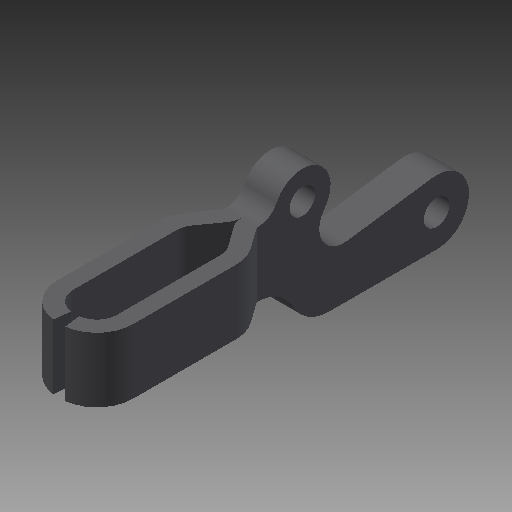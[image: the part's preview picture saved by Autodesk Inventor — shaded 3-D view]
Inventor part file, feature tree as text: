
AUTODESK INVENTOR PART (.ipt)
format: ipt  version: 2018 (Build 220112000, 112)  size: 174,592 bytes
history: native  units: mm
features: other x35, sketch x4, extrude x2, revolve x2
ambient origin geometry x8: Origin, YZ Plane, XZ Plane, XY Plane, X Axis, Y Axis, Z Axis, Center Point
bodies: Solid1 (feature_tree)
feature tree (43):
  extrude  "Extrusion1"  Depth=40.0mm TaperAngle=0.0deg
  extrude  "Extrusion2"  TaperAngle=360.0deg  [1 undecoded]
  revolve  "Revolution1"  [1 undecoded]
  revolve  "Revolution2"  [1 undecoded]
  other  "P1_XY"
  other  "P1_YZ"
  other  "P1_ZX"
  other  "P1_X"
  other  "P1_Y"
  other  "P1_Z"
  other  "P1_Center"
  other  "P2_XY"
  other  "P2_YZ"
  other  "P2_ZX"
  other  "P2_X"
  other  "P2_Y"
  other  "P2_Z"
  other  "P2_Center"
  other  "SA1_XY"
  other  "SA1_YZ"
  other  "SA1_ZX"
  other  "SA1_X"
  other  "SA1_Y"
  other  "SA1_Z"
  other  "SA1_Center"
  other  "SA2_XY"
  other  "SA2_YZ"
  other  "SA2_ZX"
  other  "SA2_X"
  other  "SA2_Y"
  other  "SA2_Z"
  other  "SA2_Center"
  other  "SA3_XY"
  other  "SA3_YZ"
  other  "SA3_ZX"
  other  "SA3_X"
  other  "SA3_Y"
  other  "SA3_Z"
  other  "SA3_Center"
  sketch  "Skizze_1"  dims[d0=40.0mm d1=0.0mm d2=40.0mm d3=0.0mm]
  sketch  "Skizze_2"
  sketch  "Skizze_3_ALT_Drilling_1"  dims[d4=360.0deg d5=360.0deg]
  sketch  "Skizze_4_ALT_Drilling_2"
note: 3 required parameter values undecoded (feature->parameter linkage not recoverable at this tier; creation-order binding heuristic only, values carry confidence <= 0.55)
